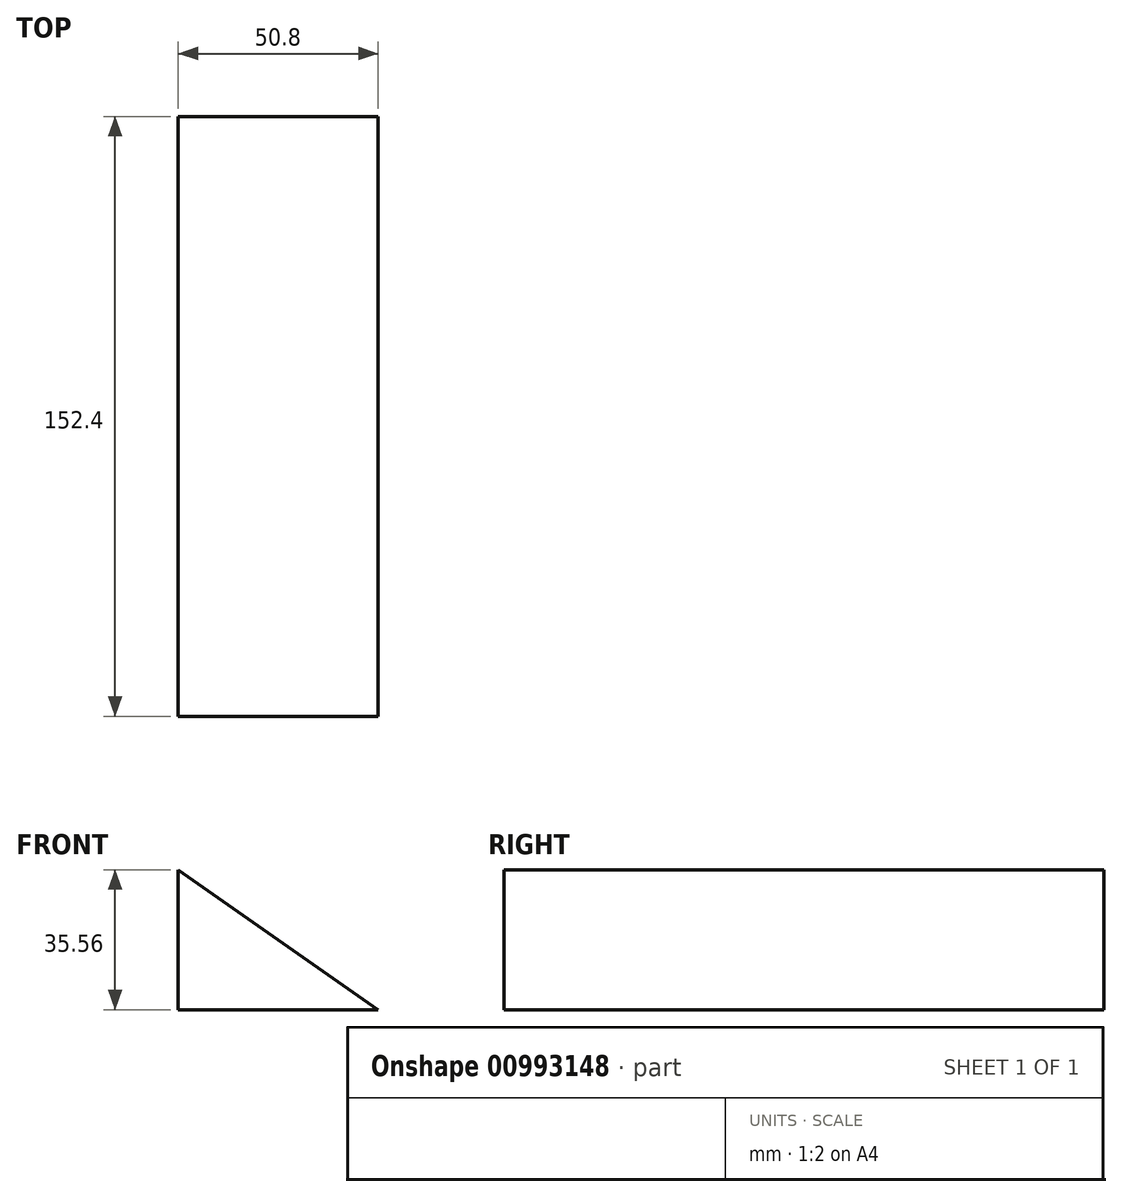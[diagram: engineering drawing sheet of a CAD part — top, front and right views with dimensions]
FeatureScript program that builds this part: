
annotation { "Feature Type Name" : "Feature", "Feature Type Description" : "" }
export const myFeature = defineFeature(function(context is Context, id is Id, definition is map)
    precondition{}
    {
        {
            var Q0;
            Q0=qCreatedBy(makeId("Right.planeOp"),FACE);
            var sketch = newSketch(context, id + "F0", { "sketchPlane" : qUnion([Q0])});
            skLineSegment(sketch, "E0.bottom", {"start": v(-100.6, 71.28) * mm, "end": v(51.8, 71.28) * mm});
            skLineSegment(sketch, "E0.top", {"start": v(-100.6, 35.72) * mm, "end": v(51.8, 35.72) * mm});
            skLineSegment(sketch, "E0.left", {"start": v(-100.6, 71.28) * mm, "end": v(-100.6, 35.72) * mm});
            skLineSegment(sketch, "E0.right", {"start": v(51.8, 71.28) * mm, "end": v(51.8, 35.72) * mm});
            skSolve(sketch);
        }
        {
            var Q0;
            Q0=makeQuery(id+"F0.imprint","IMPRINT",FACE,{"disambiguationData":[TD([[makeQuery(id+"F0.imprint","IMPRINT",EDGE,{"derivedFrom":sQuery(id+"F0.wireOp",EDGE,"E0.bottom")}),-1.0]])]});
            extrude(context, id + "F1", {"entities" : qUnion([Q0]), "depth" : 50.8 * mm, "offsetDistance" : 25.4 * mm});
        }
        {
            var Q0;
            Q0=makeQuery(id+"F1.opExtrude","SWEPT_FACE",FACE,{"disambiguationData":[OSD([sQuery(id+"F0.wireOp",EDGE,"E0.right")])]});
            var sketch = newSketch(context, id + "F2", { "sketchPlane" : qUnion([Q0])});
            skLineSegment(sketch, "E1", {"start": v(0, 71.28) * mm, "end": v(-50.8, 35.72) * mm});
            skSolve(sketch);
        }
        {
            var Q0;
            Q0=makeQuery(id+"F2.imprint","IMPRINT",FACE,{"disambiguationData":[TD([[makeQuery(id+"F2.imprint","IMPRINT",EDGE,{"derivedFrom":sQuery(id+"F2.wireOp",EDGE,"E1")}),-1.0]])]});
            extrude(context, id + "F3", {"entities" : qUnion([Q0]), "operationType" : NewBodyOperationType.REMOVE, "oppositeDirection" : true, "depth" : 203.2 * mm, "offsetDistance" : 25.4 * mm});
        }
    });
